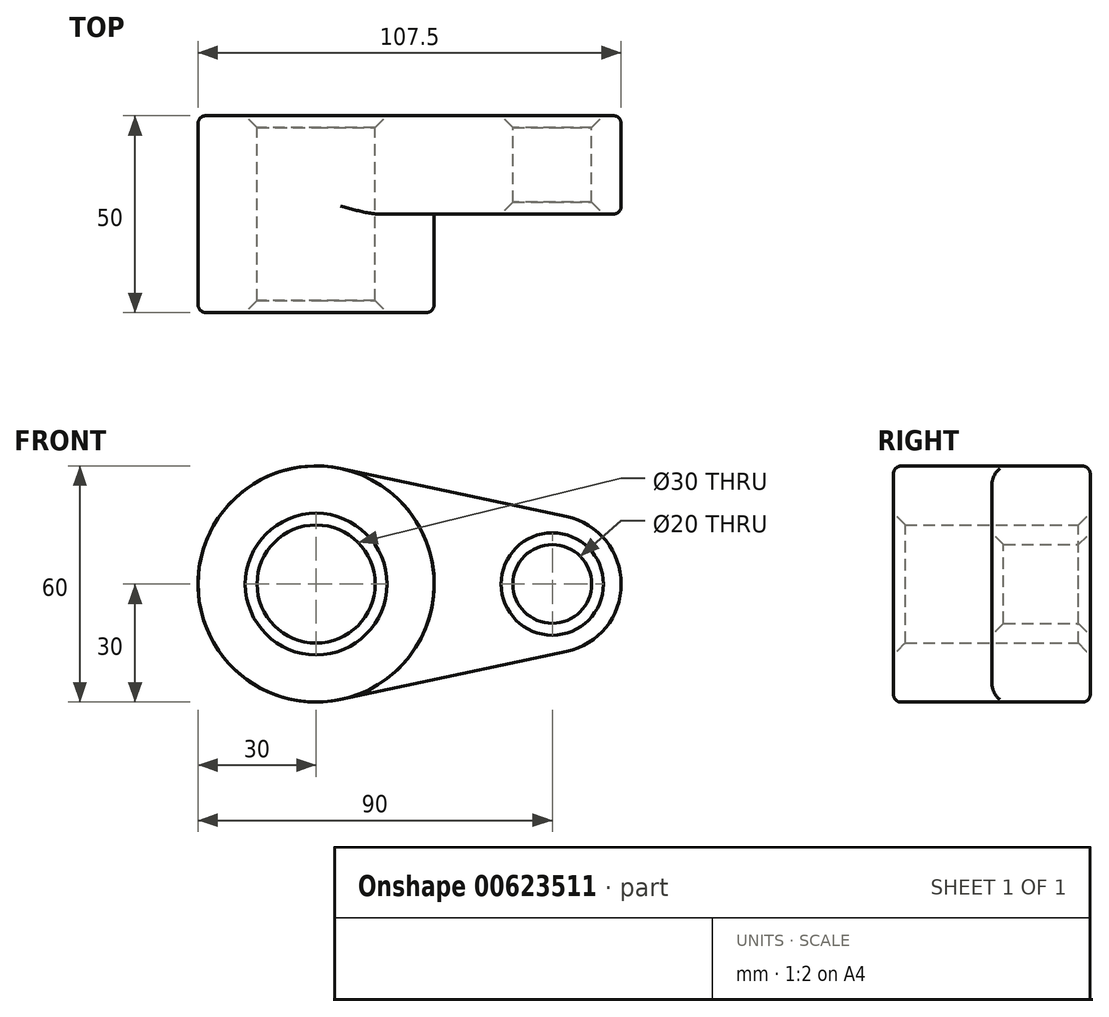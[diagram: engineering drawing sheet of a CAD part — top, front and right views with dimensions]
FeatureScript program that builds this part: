
annotation { "Feature Type Name" : "Feature", "Feature Type Description" : "" }
export const myFeature = defineFeature(function(context is Context, id is Id, definition is map)
    precondition{}
    {
        {
            var Q0;
            Q0=qCreatedBy(makeId("Front.planeOp"),FACE);
            var sketch = newSketch(context, id + "F0", { "sketchPlane" : qUnion([Q0])});
            skCircle(sketch, "E0", {"center": v(0, 0) * mm, "radius": 30 * mm});
            skCircle(sketch, "E1", {"center": v(60, 0) * mm, "radius": 17.5 * mm});
            skLineSegment(sketch, "E2", {"start": v(6.25, 29.34) * mm, "end": v(63.65, 17.12) * mm});
            skLineSegment(sketch, "E3", {"start": v(6.25, -29.34) * mm, "end": v(63.65, -17.12) * mm});
            skCircle(sketch, "E4", {"center": v(60, 0) * mm, "radius": 10 * mm});
            skCircle(sketch, "E5", {"center": v(0, 0) * mm, "radius": 15 * mm});
            skSolve(sketch);
        }
        {
            var Q0;
            Q0 = qSketchRegion(id + "F0", true);
            extrude(context, id + "F1", {"entities" : qUnion([Q0]), "depth" : 25 * mm, "offsetDistance" : 25 * mm});
        }
        {
            var Q0;
            Q0=makeQuery(id+"F0.imprint","IMPRINT",FACE,{"disambiguationData":[TD([[makeQuery(id+"F0.imprint","IMPRINT",EDGE,{"derivedFrom":sQuery(id+"F0.wireOp",EDGE,"E5")}),-1.0]])]});
            extrude(context, id + "F2", {"entities" : qUnion([Q0]), "operationType" : NewBodyOperationType.ADD, "depth" : 50 * mm, "offsetDistance" : 25 * mm});
        }
        {
            var Q0;
            Q0=makeQuery(id+"F1.opExtrude","CAP_EDGE",EDGE,{"disambiguationData":[OSD([sQuery(id+"F0.wireOp",EDGE,"E3")])],"isStart":false});
            var Q1;
            Q1=makeQuery(id+"F1.opExtrude","CAP_EDGE",EDGE,{"disambiguationData":[OSD([sQuery(id+"F0.wireOp",EDGE,"E3")])],"isStart":true});
            fillet(context, id + "F3", {"entities" : qUnion([Q0, Q1]), "radius" : 2 * mm, "tangentPropagation" : true, "allowEdgeOverflow" : false});
        }
        {
            var Q0;
            Q0=makeQuery(id+"F2.opExtrude","CAP_EDGE",EDGE,{"disambiguationData":[OSD([sQuery(id+"F0.wireOp",EDGE,"E0")])],"isStart":false});
            fillet(context, id + "F4", {"entities" : qUnion([Q0]), "radius" : 2 * mm, "tangentPropagation" : true, "allowEdgeOverflow" : false});
        }
        {
            var Q0;
            Q0=makeQuery(id+"F2.opExtrude","CAP_EDGE",EDGE,{"disambiguationData":[OSD([sQuery(id+"F0.wireOp",EDGE,"E5")])],"isStart":false});
            var Q1;
            Q1=makeQuery(id+"F1.opExtrude","CAP_EDGE",EDGE,{"disambiguationData":[OSD([sQuery(id+"F0.wireOp",EDGE,"E4")])],"isStart":false});
            chamfer(context, id + "F5", {"entities" : qUnion([Q0, Q1]), "width" : 3 * mm, "tangentPropagation" : true});
        }
        {
            var Q0;
            Q0=makeQuery(id+"F1.opExtrude","CAP_EDGE",EDGE,{"disambiguationData":[OSD([sQuery(id+"F0.wireOp",EDGE,"E5")])],"isStart":true});
            var Q1;
            Q1=makeQuery(id+"F1.opExtrude","CAP_EDGE",EDGE,{"disambiguationData":[OSD([sQuery(id+"F0.wireOp",EDGE,"E4")])],"isStart":true});
            chamfer(context, id + "F6", {"entities" : qUnion([Q0, Q1]), "width" : 3 * mm, "tangentPropagation" : true});
        }
    });
